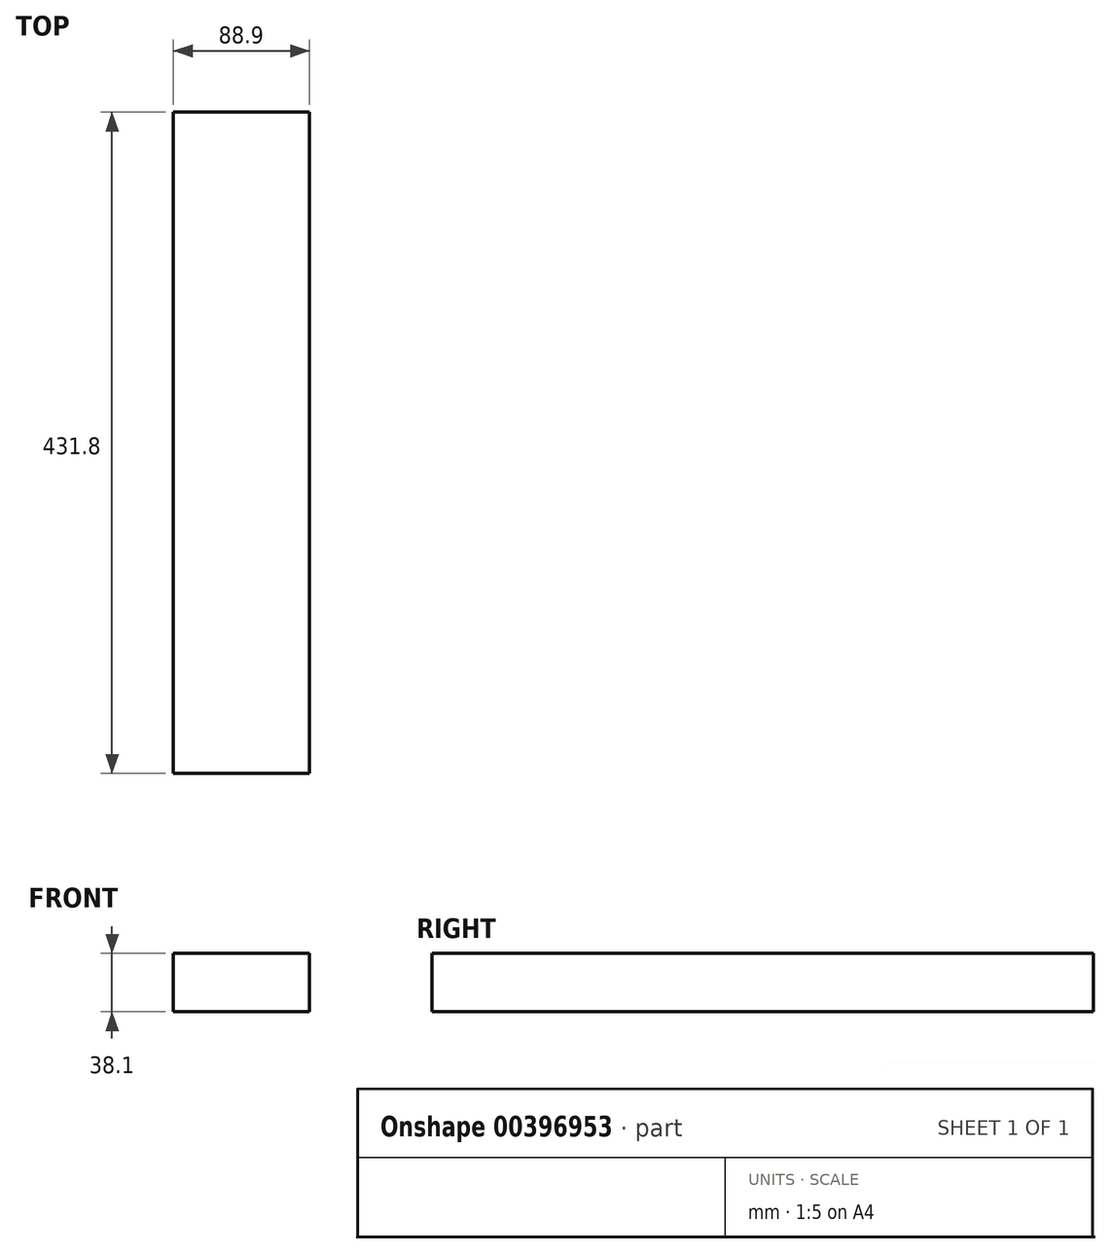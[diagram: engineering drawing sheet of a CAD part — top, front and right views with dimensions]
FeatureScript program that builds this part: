
annotation { "Feature Type Name" : "Feature", "Feature Type Description" : "" }
export const myFeature = defineFeature(function(context is Context, id is Id, definition is map)
    precondition{}
    {
        {
            var Q0;
            Q0=qCreatedBy(makeId("Front.planeOp"),FACE);
            var sketch = newSketch(context, id + "F0", { "sketchPlane" : qUnion([Q0])});
            skLineSegment(sketch, "E0.bottom", {"start": v(44.45, 19.05) * mm, "end": v(-44.45, 19.05) * mm});
            skLineSegment(sketch, "E0.top", {"start": v(44.45, -19.05) * mm, "end": v(-44.45, -19.05) * mm});
            skLineSegment(sketch, "E0.left", {"start": v(44.45, 19.05) * mm, "end": v(44.45, -19.05) * mm});
            skLineSegment(sketch, "E0.right", {"start": v(-44.45, 19.05) * mm, "end": v(-44.45, -19.05) * mm});
            skPoint(sketch, "E0.middle", {"position": v(0, 0) * mm});
            skSolve(sketch);
        }
        {
            var Q0;
            Q0 = qSketchRegion(id + "F0", true);
            extrude(context, id + "F1", {"entities" : qUnion([Q0]), "depth" : 431.8 * mm});
        }
    });
